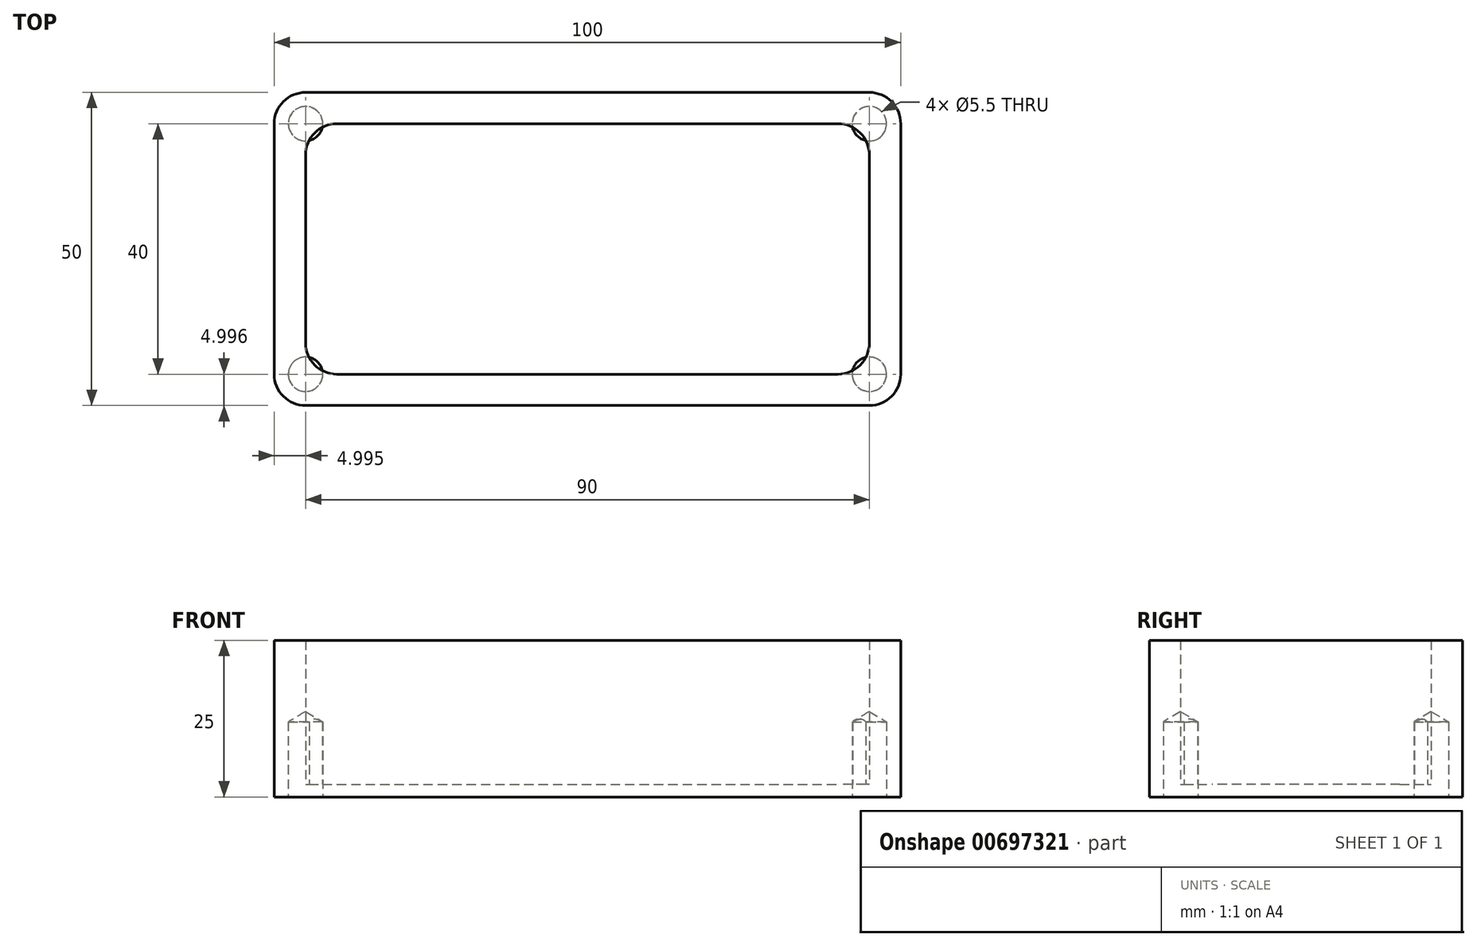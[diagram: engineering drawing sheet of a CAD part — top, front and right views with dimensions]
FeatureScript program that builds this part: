
annotation { "Feature Type Name" : "Feature", "Feature Type Description" : "" }
export const myFeature = defineFeature(function(context is Context, id is Id, definition is map)
    precondition{}
    {
        {
            var Q0;
            Q0=qCreatedBy(makeId("Top.planeOp"),FACE);
            var sketch = newSketch(context, id + "F0", { "sketchPlane" : qUnion([Q0])});
            skLineSegment(sketch, "E0.bottom", {"start": v(-43.52, 16.13) * mm, "end": v(56.48, 16.13) * mm});
            skLineSegment(sketch, "E0.top", {"start": v(-43.52, -33.87) * mm, "end": v(56.48, -33.87) * mm});
            skLineSegment(sketch, "E0.left", {"start": v(-43.52, 16.13) * mm, "end": v(-43.52, -33.87) * mm});
            skLineSegment(sketch, "E0.right", {"start": v(56.48, 16.13) * mm, "end": v(56.48, -33.87) * mm});
            skLineSegment(sketch, "E1.bottom", {"start": v(-33.52, 11.13) * mm, "end": v(46.48, 11.13) * mm});
            skLineSegment(sketch, "E1.top", {"start": v(-33.52, -28.87) * mm, "end": v(46.48, -28.87) * mm});
            skLineSegment(sketch, "E1.left", {"start": v(-38.52, 6.13) * mm, "end": v(-38.52, -23.87) * mm});
            skLineSegment(sketch, "E1.right", {"start": v(51.48, 6.13) * mm, "end": v(51.48, -23.87) * mm});
            skPoint(sketch, "E2.visualSharp", {"position": v(-38.52, 11.13) * mm});
            skArc(sketch, "E2.filletArc", {"start": v(-33.52, 11.13) * mm, "mid": v(-37.06, 9.66) * mm, "end": v(-38.52, 6.13) * mm});
            skPoint(sketch, "E3.visualSharp", {"position": v(51.48, 11.13) * mm});
            skArc(sketch, "E3.filletArc", {"start": v(51.48, 6.13) * mm, "mid": v(50.01, 9.66) * mm, "end": v(46.48, 11.13) * mm});
            skPoint(sketch, "E4.visualSharp", {"position": v(51.48, -28.87) * mm});
            skArc(sketch, "E4.filletArc", {"start": v(46.48, -28.87) * mm, "mid": v(50.01, -27.4) * mm, "end": v(51.48, -23.87) * mm});
            skPoint(sketch, "E5.visualSharp", {"position": v(-38.52, -28.87) * mm});
            skArc(sketch, "E5.filletArc", {"start": v(-38.52, -23.87) * mm, "mid": v(-37.06, -27.4) * mm, "end": v(-33.52, -28.87) * mm});
            skSolve(sketch);
        }
        {
            var Q0;
            Q0=makeQuery(id+"F0.imprint","IMPRINT",FACE,{"disambiguationData":[TD([[makeQuery(id+"F0.imprint","IMPRINT",EDGE,{"derivedFrom":sQuery(id+"F0.wireOp",EDGE,"E0.bottom")}),-1.0]])]});
            extrude(context, id + "F1", {"entities" : qUnion([Q0]), "depth" : 25 * mm, "offsetDistance" : 25 * mm});
        }
        {
            var Q0;
            Q0=makeQuery(id+"F0.imprint","IMPRINT",FACE,{"disambiguationData":[TD([[makeQuery(id+"F0.imprint","IMPRINT",EDGE,{"derivedFrom":sQuery(id+"F0.wireOp",EDGE,"E0.bottom")}),-1.0]])]});
            var Q1;
            Q1=makeQuery(id+"F0.imprint","IMPRINT",FACE,{"disambiguationData":[TD([[makeQuery(id+"F0.imprint","IMPRINT",EDGE,{"derivedFrom":sQuery(id+"F0.wireOp",EDGE,"E1.bottom")}),-1.0]])]});
            extrude(context, id + "F2", {"entities" : qUnion([Q0, Q1]), "operationType" : NewBodyOperationType.ADD, "depth" : 2 * mm, "offsetDistance" : 25 * mm});
        }
        {
            var Q0;
            Q0=makeQuery(id+"F1.opExtrude","SWEPT_EDGE",EDGE,{"disambiguationData":[OSD([sQuery(id+"F0.wireOp",EDGE,"E0.top"),sQuery(id+"F0.wireOp",EDGE,"E0.left")])]});
            var Q1;
            Q1=makeQuery(id+"F1.opExtrude","SWEPT_EDGE",EDGE,{"disambiguationData":[OSD([sQuery(id+"F0.wireOp",EDGE,"E0.top"),sQuery(id+"F0.wireOp",EDGE,"E0.right")])]});
            var Q2;
            Q2=makeQuery(id+"F1.opExtrude","SWEPT_EDGE",EDGE,{"disambiguationData":[OSD([sQuery(id+"F0.wireOp",EDGE,"E0.bottom"),sQuery(id+"F0.wireOp",EDGE,"E0.right")])]});
            var Q3;
            Q3=makeQuery(id+"F1.opExtrude","SWEPT_EDGE",EDGE,{"disambiguationData":[OSD([sQuery(id+"F0.wireOp",EDGE,"E0.bottom"),sQuery(id+"F0.wireOp",EDGE,"E0.left")])]});
            fillet(context, id + "F3", {"entities" : qUnion([Q0, Q1, Q2, Q3]), "radius" : 5 * mm, "tangentPropagation" : true, "allowEdgeOverflow" : false});
        }
        {
            var Q0;
            Q0=sQuery(id+"F0.wireOp",VERTEX,"E3.visualSharp");
            var Q1;
            Q1=sQuery(id+"F0.wireOp",VERTEX,"E4.visualSharp");
            var Q2;
            Q2=sQuery(id+"F0.wireOp",VERTEX,"E5.visualSharp");
            var Q3;
            Q3=sQuery(id+"F0.wireOp",VERTEX,"E2.visualSharp");
            var Q4;
            Q4=makeQuery(id+"F1.opExtrude","SWEPT_BODY",BODY,{"disambiguationData":[OSD([sQuery(id+"F0.wireOp",EDGE,"E0.bottom"),sQuery(id+"F0.wireOp",EDGE,"E0.top"),sQuery(id+"F0.wireOp",EDGE,"E0.left"),sQuery(id+"F0.wireOp",EDGE,"E0.right"),sQuery(id+"F0.wireOp",EDGE,"E1.bottom"),sQuery(id+"F0.wireOp",EDGE,"E1.top"),sQuery(id+"F0.wireOp",EDGE,"E1.left"),sQuery(id+"F0.wireOp",EDGE,"E1.right"),sQuery(id+"F0.wireOp",EDGE,"E2.filletArc"),sQuery(id+"F0.wireOp",EDGE,"E3.filletArc"),sQuery(id+"F0.wireOp",EDGE,"E4.filletArc"),sQuery(id+"F0.wireOp",EDGE,"E5.filletArc")])]});
            hole(context, id + "F4", {"style" : HoleStyle.SIMPLE, "endStyle" : HoleEndStyle.BLIND, "oppositeDirection" : true, "standardTappedOrClearance" : lookupTablePath({ "standard" : "ISO", "fit" : "Normal", "size" : "M5", "type" : "Clearance" }), "standardBlindInLast" : lookupTablePath({ "fit" : "Standard", "standard" : "ISO", "size" : "M5", "type" : "Clearance" }), "holeDiameter" : 5.5 * mm, "majorDiameter" : 5 * mm, "holeDepth" : 12 * mm, "isTappedThrough" : true, "tappedDepth" : 12 * mm, "tapClearance" : 3, "startFromSketch" : true, "locations" : qUnion([Q0, Q1, Q2, Q3]), "scope" : qUnion([Q4])});
        }
    });
